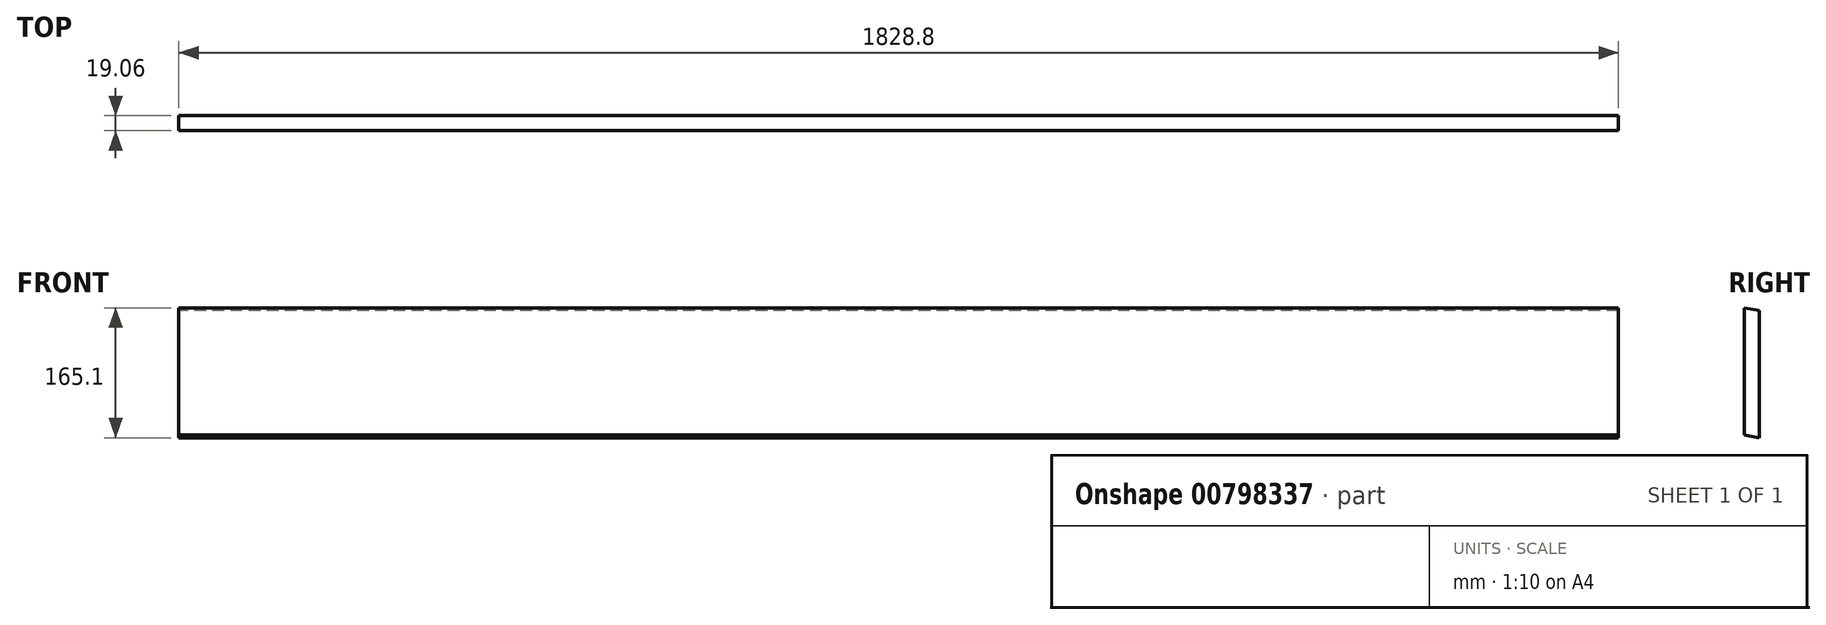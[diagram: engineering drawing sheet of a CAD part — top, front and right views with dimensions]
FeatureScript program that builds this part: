
annotation { "Feature Type Name" : "Feature", "Feature Type Description" : "" }
export const myFeature = defineFeature(function(context is Context, id is Id, definition is map)
    precondition{}
    {
        {
            var Q0;
            Q0=qCreatedBy(makeId("Right.planeOp"),FACE);
            var sketch = newSketch(context, id + "F0", { "sketchPlane" : qUnion([Q0])});
            skLineSegment(sketch, "E0.left", {"start": v(9.53, 79.2) * mm, "end": v(9.53, -82.55) * mm});
            skLineSegment(sketch, "E0.right", {"start": v(-9.52, 82.55) * mm, "end": v(-9.53, -79.2) * mm});
            skPoint(sketch, "E0.middle", {"position": v(0, 0) * mm});
            skLineSegment(sketch, "E1", {"start": v(9.53, -82.55) * mm, "end": v(-9.53, -79.2) * mm});
            skPoint(sketch, "E2.orphan", {"position": v(-9.53, -101.6) * mm});
            skLineSegment(sketch, "E3", {"start": v(-9.53, 82.55) * mm, "end": v(9.52, 79.2) * mm});
            skPoint(sketch, "E4.orphan", {"position": v(9.53, 101.6) * mm});
            skSolve(sketch);
        }
        {
            var Q0;
            Q0 = qSketchRegion(id + "F0", true);
            extrude(context, id + "F1", {"entities" : qUnion([Q0]), "depth" : 1828.8 * mm, "offsetDistance" : 25.4 * mm});
        }
    });
